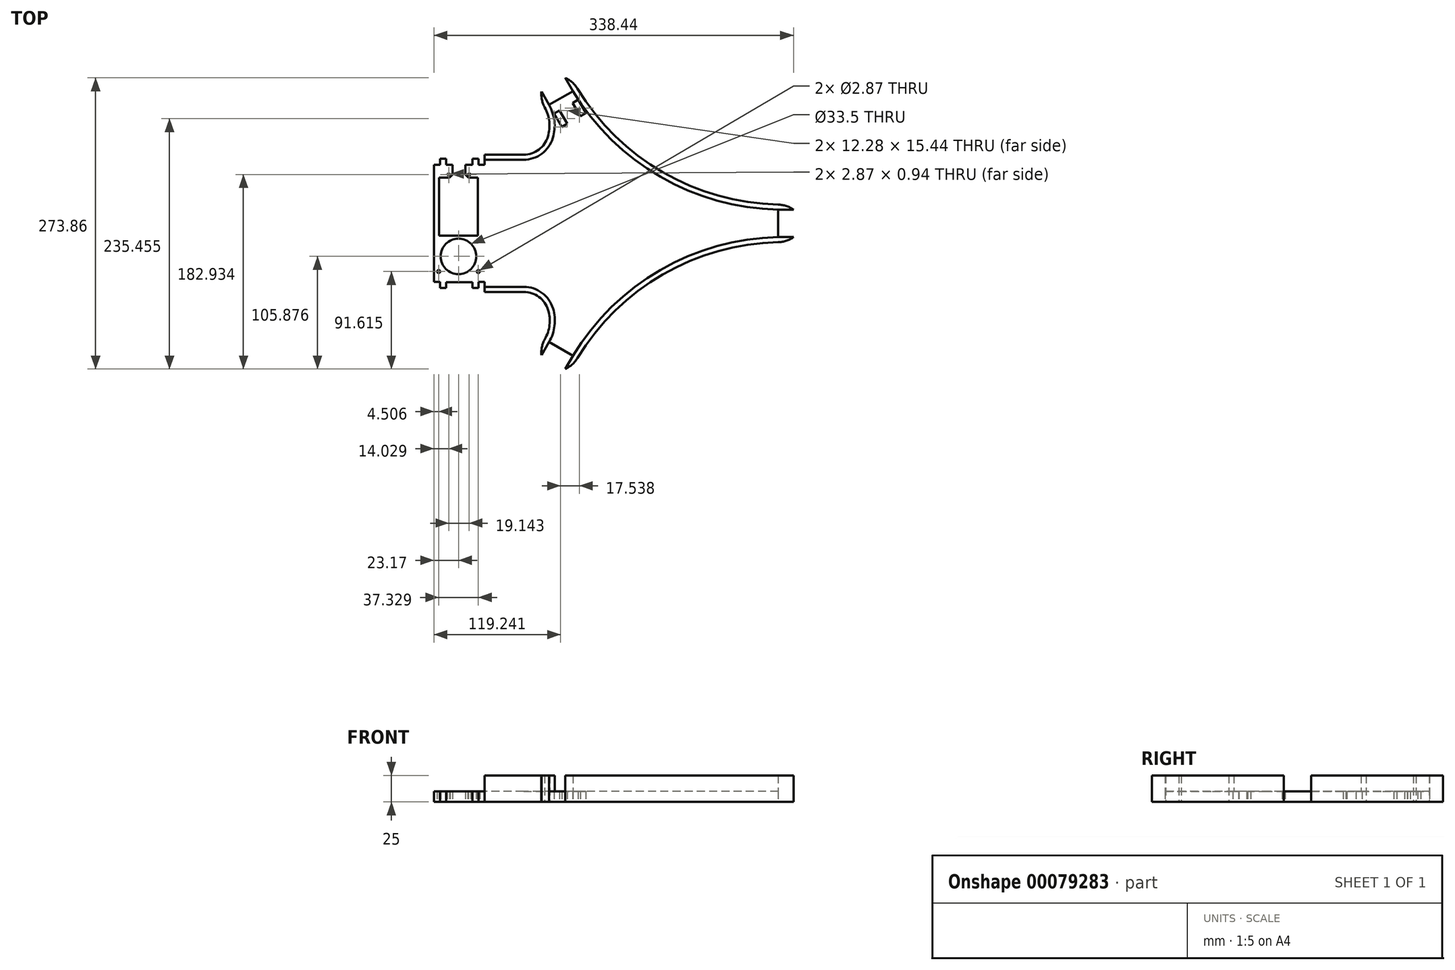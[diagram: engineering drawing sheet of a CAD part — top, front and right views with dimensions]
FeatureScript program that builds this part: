
annotation { "Feature Type Name" : "Feature", "Feature Type Description" : "" }
export const myFeature = defineFeature(function(context is Context, id is Id, definition is map)
    precondition{}
    {
        {
            var Q0;
            Q0=qCreatedBy(makeId("Top.planeOp"),FACE);
            var sketch = newSketch(context, id + "F0", { "sketchPlane" : qUnion([Q0])});
            skLineSegment(sketch, "E0", {"start": v(154.86, 12.92) * mm, "end": v(154.86, -12.92) * mm});
            skLineSegment(sketch, "E1", {"start": v(169.22, -12.92) * mm, "end": v(154.86, -12.92) * mm});
            skArc(sketch, "E2", {"start": v(154.86, -17.7) * mm, "mid": v(162.4, -16.4) * mm, "end": v(169.22, -12.92) * mm});
            skArc(sketch, "E3", {"start": v(154.86, -17.7) * mm, "mid": v(46.3, -48.05) * mm, "end": v(-34.25, -126.9) * mm});
            skArc(sketch, "E4", {"start": v(-45.57, -136.93) * mm, "mid": v(-39.15, -132.77) * mm, "end": v(-34.25, -126.9) * mm});
            skLineSegment(sketch, "E5", {"start": v(-45.57, -136.93) * mm, "end": v(-38.4, -124.5) * mm});
            skLineSegment(sketch, "E6", {"start": v(-38.4, -124.5) * mm, "end": v(-60.78, -111.58) * mm});
            skLineSegment(sketch, "E7", {"start": v(-67.95, -124.01) * mm, "end": v(-60.78, -111.58) * mm});
            skArc(sketch, "E8", {"start": v(-64.92, -109.18) * mm, "mid": v(-67.56, -116.37) * mm, "end": v(-67.95, -124.01) * mm});
            skArc(sketch, "E9", {"start": v(-64.92, -109.18) * mm, "mid": v(-60.4, -95.67) * mm, "end": v(-61.68, -81.48) * mm});
            skArc(sketch, "E10", {"start": v(-61.68, -81.48) * mm, "mid": v(-70.33, -69.23) * mm, "end": v(-84.57, -64.54) * mm});
            skLineSegment(sketch, "E11", {"start": v(-97.94, -64.54) * mm, "end": v(-84.57, -64.54) * mm});
            skLineSegment(sketch, "E12", {"start": v(-97.94, -64.54) * mm, "end": v(-121.43, -64.54) * mm});
            skLineSegment(sketch, "E13", {"start": v(-121.43, -55.04) * mm, "end": v(-121.43, -64.54) * mm});
            skLineSegment(sketch, "E14", {"start": v(-127.17, -55.04) * mm, "end": v(-121.43, -55.04) * mm});
            skLineSegment(sketch, "E15", {"start": v(-127.17, -60.78) * mm, "end": v(-127.17, -55.04) * mm});
            skLineSegment(sketch, "E16", {"start": v(-132.92, -60.78) * mm, "end": v(-127.17, -60.78) * mm});
            skLineSegment(sketch, "E17", {"start": v(-132.92, -55.45) * mm, "end": v(-132.92, -60.78) * mm});
            skLineSegment(sketch, "E18", {"start": v(-157.73, -55.45) * mm, "end": v(-132.92, -55.45) * mm});
            skLineSegment(sketch, "E19", {"start": v(-157.73, -55.45) * mm, "end": v(-157.73, -60.78) * mm});
            skLineSegment(sketch, "E20", {"start": v(-157.73, -60.78) * mm, "end": v(-163.48, -60.78) * mm});
            skLineSegment(sketch, "E21", {"start": v(-163.48, -60.78) * mm, "end": v(-163.48, -55.04) * mm});
            skLineSegment(sketch, "E22", {"start": v(-169.22, -55.04) * mm, "end": v(-163.48, -55.04) * mm});
            skLineSegment(sketch, "E23", {"start": v(-169.22, 55.04) * mm, "end": v(-169.22, -55.04) * mm});
            skLineSegment(sketch, "E24", {"start": v(-163.48, 55.04) * mm, "end": v(-169.22, 55.04) * mm});
            skLineSegment(sketch, "E25", {"start": v(-163.48, 60.78) * mm, "end": v(-163.48, 55.04) * mm});
            skLineSegment(sketch, "E26", {"start": v(-157.73, 60.78) * mm, "end": v(-163.48, 60.78) * mm});
            skLineSegment(sketch, "E27", {"start": v(-157.73, 55.04) * mm, "end": v(-157.73, 60.78) * mm});
            skLineSegment(sketch, "E28", {"start": v(-151.6, 55.04) * mm, "end": v(-157.73, 55.04) * mm});
            skLineSegment(sketch, "E29", {"start": v(-151.6, 50.17) * mm, "end": v(-151.6, 55.04) * mm});
            skLineSegment(sketch, "E30", {"start": v(-151.6, 50.17) * mm, "end": v(-151.6, 46) * mm});
            skArc(sketch, "E31", {"start": v(-154.47, 43.13) * mm, "mid": v(-152.44, 43.97) * mm, "end": v(-151.6, 46) * mm});
            skLineSegment(sketch, "E32", {"start": v(-164.24, 43.13) * mm, "end": v(-154.47, 43.13) * mm});
            skLineSegment(sketch, "E33", {"start": v(-164.24, -11.43) * mm, "end": v(-164.24, 43.13) * mm});
            skLineSegment(sketch, "E34", {"start": v(-127.86, -11.43) * mm, "end": v(-164.24, -11.43) * mm});
            skLineSegment(sketch, "E35", {"start": v(-127.86, 43.13) * mm, "end": v(-127.86, -11.43) * mm});
            skLineSegment(sketch, "E36", {"start": v(-136.77, 43.13) * mm, "end": v(-127.86, 43.13) * mm});
            skArc(sketch, "E37", {"start": v(-139.64, 46) * mm, "mid": v(-138.8, 43.97) * mm, "end": v(-136.77, 43.13) * mm});
            skLineSegment(sketch, "E38", {"start": v(-139.64, 46) * mm, "end": v(-139.64, 50.17) * mm});
            skLineSegment(sketch, "E39", {"start": v(-139.64, 50.17) * mm, "end": v(-139.64, 55.04) * mm});
            skLineSegment(sketch, "E40", {"start": v(-132.92, 55.04) * mm, "end": v(-139.64, 55.04) * mm});
            skLineSegment(sketch, "E41", {"start": v(-132.92, 55.04) * mm, "end": v(-132.92, 60.78) * mm});
            skLineSegment(sketch, "E42", {"start": v(-132.92, 60.78) * mm, "end": v(-127.17, 60.78) * mm});
            skLineSegment(sketch, "E43", {"start": v(-127.17, 60.78) * mm, "end": v(-127.17, 55.04) * mm});
            skLineSegment(sketch, "E44", {"start": v(-121.43, 55.04) * mm, "end": v(-127.17, 55.04) * mm});
            skLineSegment(sketch, "E45", {"start": v(-121.43, 64.68) * mm, "end": v(-121.43, 55.04) * mm});
            skLineSegment(sketch, "E46", {"start": v(-97.94, 64.68) * mm, "end": v(-121.43, 64.68) * mm});
            skLineSegment(sketch, "E47", {"start": v(-97.94, 64.68) * mm, "end": v(-84.8, 64.68) * mm});
            skArc(sketch, "E48", {"start": v(-84.8, 64.68) * mm, "mid": v(-70.5, 69.41) * mm, "end": v(-61.87, 81.74) * mm});
            skArc(sketch, "E49", {"start": v(-61.87, 81.74) * mm, "mid": v(-60.6, 95.77) * mm, "end": v(-64.92, 109.18) * mm});
            skArc(sketch, "E50", {"start": v(-67.95, 124.01) * mm, "mid": v(-67.56, 116.37) * mm, "end": v(-64.92, 109.18) * mm});
            skLineSegment(sketch, "E51", {"start": v(-67.95, 124.01) * mm, "end": v(-60.78, 111.58) * mm});
            skLineSegment(sketch, "E52", {"start": v(-60.78, 111.58) * mm, "end": v(-38.4, 124.5) * mm});
            skLineSegment(sketch, "E53", {"start": v(-45.57, 136.93) * mm, "end": v(-38.4, 124.5) * mm});
            skArc(sketch, "E54", {"start": v(-34.25, 126.9) * mm, "mid": v(-39.15, 132.77) * mm, "end": v(-45.57, 136.93) * mm});
            skArc(sketch, "E55", {"start": v(-34.25, 126.9) * mm, "mid": v(46.3, 48.05) * mm, "end": v(154.86, 17.7) * mm});
            skArc(sketch, "E56", {"start": v(169.22, 12.92) * mm, "mid": v(162.4, 16.4) * mm, "end": v(154.86, 17.7) * mm});
            skLineSegment(sketch, "E57", {"start": v(169.22, 12.92) * mm, "end": v(154.86, 12.92) * mm});
            skLineSegment(sketch, "E58", {"start": v(145.3, -13.02) * mm, "end": v(130.84, -13.02) * mm, "construction": true});
            skLineSegment(sketch, "E59", {"start": v(130.84, -13.02) * mm, "end": v(130.84, -7.18) * mm, "construction": true});
            skLineSegment(sketch, "E60", {"start": v(130.84, -7.18) * mm, "end": v(145.3, -7.18) * mm, "construction": true});
            skLineSegment(sketch, "E61", {"start": v(145.3, -7.18) * mm, "end": v(145.3, -13.02) * mm, "construction": true});
            skLineSegment(sketch, "E62", {"start": v(102.12, -13.02) * mm, "end": v(87.67, -13.02) * mm, "construction": true});
            skLineSegment(sketch, "E63", {"start": v(87.67, -13.02) * mm, "end": v(87.67, -7.18) * mm, "construction": true});
            skLineSegment(sketch, "E64", {"start": v(87.67, -7.18) * mm, "end": v(102.12, -7.18) * mm, "construction": true});
            skLineSegment(sketch, "E65", {"start": v(102.12, -7.18) * mm, "end": v(102.12, -13.02) * mm, "construction": true});
            skLineSegment(sketch, "E66", {"start": v(145.39, 13.02) * mm, "end": v(130.93, 13.02) * mm, "construction": true});
            skLineSegment(sketch, "E67", {"start": v(130.93, 13.02) * mm, "end": v(130.93, 7.18) * mm, "construction": true});
            skLineSegment(sketch, "E68", {"start": v(130.93, 7.18) * mm, "end": v(145.39, 7.18) * mm, "construction": true});
            skLineSegment(sketch, "E69", {"start": v(145.39, 7.18) * mm, "end": v(145.39, 13.02) * mm, "construction": true});
            skLineSegment(sketch, "E70", {"start": v(102.32, 13.02) * mm, "end": v(87.86, 13.02) * mm, "construction": true});
            skLineSegment(sketch, "E71", {"start": v(87.86, 13.02) * mm, "end": v(87.86, 7.18) * mm, "construction": true});
            skLineSegment(sketch, "E72", {"start": v(87.86, 7.18) * mm, "end": v(102.32, 7.18) * mm, "construction": true});
            skLineSegment(sketch, "E73", {"start": v(102.32, 7.18) * mm, "end": v(102.32, 13.02) * mm, "construction": true});
            skLineSegment(sketch, "E74", {"start": v(-76.97, 60.88) * mm, "end": v(-94.2, 60.88) * mm, "construction": true});
            skLineSegment(sketch, "E75", {"start": v(-94.2, 60.88) * mm, "end": v(-94.2, 55.04) * mm, "construction": true});
            skLineSegment(sketch, "E76", {"start": v(-94.2, 55.04) * mm, "end": v(-76.97, 55.04) * mm, "construction": true});
            skLineSegment(sketch, "E77", {"start": v(-76.97, 55.04) * mm, "end": v(-76.97, 60.88) * mm, "construction": true});
            skLineSegment(sketch, "E78", {"start": v(-76.97, -55.04) * mm, "end": v(-94.2, -55.04) * mm, "construction": true});
            skLineSegment(sketch, "E79", {"start": v(-94.2, -55.04) * mm, "end": v(-94.2, -60.88) * mm, "construction": true});
            skLineSegment(sketch, "E80", {"start": v(-94.2, -60.88) * mm, "end": v(-76.97, -60.88) * mm, "construction": true});
            skLineSegment(sketch, "E81", {"start": v(-76.97, -60.88) * mm, "end": v(-76.97, -55.04) * mm, "construction": true});
            skLineSegment(sketch, "E82", {"start": v(79.25, -1.44) * mm, "end": v(96.48, -1.44) * mm, "construction": true});
            skLineSegment(sketch, "E83", {"start": v(96.48, -1.44) * mm, "end": v(96.48, 1.44) * mm, "construction": true});
            skLineSegment(sketch, "E84", {"start": v(96.48, 1.44) * mm, "end": v(79.25, 1.44) * mm, "construction": true});
            skLineSegment(sketch, "E85", {"start": v(79.25, 1.44) * mm, "end": v(79.25, -1.44) * mm, "construction": true});
            skLineSegment(sketch, "E86", {"start": v(-137.48, 46.48) * mm, "end": v(-137.48, 45.53) * mm});
            skLineSegment(sketch, "E87", {"start": v(-137.48, 45.53) * mm, "end": v(-134.61, 45.53) * mm});
            skLineSegment(sketch, "E88", {"start": v(-134.61, 45.53) * mm, "end": v(-134.61, 46.48) * mm});
            skLineSegment(sketch, "E89", {"start": v(-134.61, 46.48) * mm, "end": v(-137.48, 46.48) * mm});
            skLineSegment(sketch, "E90", {"start": v(-156.63, 46.48) * mm, "end": v(-156.63, 45.53) * mm});
            skLineSegment(sketch, "E91", {"start": v(-156.63, 45.53) * mm, "end": v(-153.76, 45.53) * mm});
            skLineSegment(sketch, "E92", {"start": v(-153.76, 45.53) * mm, "end": v(-153.76, 46.48) * mm});
            skLineSegment(sketch, "E93", {"start": v(-153.76, 46.48) * mm, "end": v(-156.63, 46.48) * mm});
            skLineSegment(sketch, "E94", {"start": v(-34.48, 41.88) * mm, "end": v(-37.35, 44.75) * mm, "construction": true});
            skLineSegment(sketch, "E95", {"start": v(-37.35, 44.75) * mm, "end": v(-39.45, 44.75) * mm, "construction": true});
            skLineSegment(sketch, "E96", {"start": v(-39.45, 44.75) * mm, "end": v(-42.32, 47.62) * mm, "construction": true});
            skLineSegment(sketch, "E97", {"start": v(-42.32, 47.62) * mm, "end": v(-42.32, 49.63) * mm, "construction": true});
            skLineSegment(sketch, "E98", {"start": v(-42.32, 49.63) * mm, "end": v(-45.19, 52.5) * mm, "construction": true});
            skLineSegment(sketch, "E99", {"start": v(-45.19, 52.5) * mm, "end": v(-72.18, 52.5) * mm, "construction": true});
            skLineSegment(sketch, "E100", {"start": v(-72.18, 52.5) * mm, "end": v(-75.05, 49.63) * mm, "construction": true});
            skLineSegment(sketch, "E101", {"start": v(-75.05, 49.63) * mm, "end": v(-75.05, -49.63) * mm, "construction": true});
            skLineSegment(sketch, "E102", {"start": v(-75.05, -49.63) * mm, "end": v(-72.18, -52.5) * mm, "construction": true});
            skLineSegment(sketch, "E103", {"start": v(-72.18, -52.5) * mm, "end": v(-45.19, -52.5) * mm, "construction": true});
            skLineSegment(sketch, "E104", {"start": v(-45.19, -52.5) * mm, "end": v(-42.32, -49.63) * mm, "construction": true});
            skLineSegment(sketch, "E105", {"start": v(-42.32, -49.63) * mm, "end": v(-42.32, -47.62) * mm, "construction": true});
            skLineSegment(sketch, "E106", {"start": v(-42.32, -47.62) * mm, "end": v(-39.45, -44.75) * mm, "construction": true});
            skLineSegment(sketch, "E107", {"start": v(-39.45, -44.75) * mm, "end": v(-37.35, -44.75) * mm, "construction": true});
            skLineSegment(sketch, "E108", {"start": v(-37.35, -44.75) * mm, "end": v(-34.48, -41.88) * mm, "construction": true});
            skLineSegment(sketch, "E109", {"start": v(-34.48, -41.88) * mm, "end": v(-34.48, 41.88) * mm, "construction": true});
            skLineSegment(sketch, "E110", {"start": v(-103.77, 42.88) * mm, "end": v(-103.77, 49.63) * mm, "construction": true});
            skLineSegment(sketch, "E111", {"start": v(-103.77, 49.63) * mm, "end": v(-100.9, 52.5) * mm, "construction": true});
            skLineSegment(sketch, "E112", {"start": v(-100.9, 52.5) * mm, "end": v(-97.07, 52.5) * mm, "construction": true});
            skLineSegment(sketch, "E113", {"start": v(-97.07, 52.5) * mm, "end": v(-94.2, 49.63) * mm, "construction": true});
            skLineSegment(sketch, "E114", {"start": v(-94.2, 49.63) * mm, "end": v(-94.2, 42.88) * mm, "construction": true});
            skLineSegment(sketch, "E115", {"start": v(-94.2, 42.88) * mm, "end": v(-97.07, 40) * mm, "construction": true});
            skLineSegment(sketch, "E116", {"start": v(-97.07, 40) * mm, "end": v(-100.9, 40) * mm, "construction": true});
            skLineSegment(sketch, "E117", {"start": v(-100.9, 40) * mm, "end": v(-103.77, 42.88) * mm, "construction": true});
            skLineSegment(sketch, "E118", {"start": v(-103.77, 29.48) * mm, "end": v(-100.9, 32.35) * mm, "construction": true});
            skLineSegment(sketch, "E119", {"start": v(-100.9, 32.35) * mm, "end": v(-97.07, 32.35) * mm, "construction": true});
            skLineSegment(sketch, "E120", {"start": v(-97.07, 32.35) * mm, "end": v(-94.2, 29.48) * mm, "construction": true});
            skLineSegment(sketch, "E121", {"start": v(-94.2, 29.48) * mm, "end": v(-94.2, -41.88) * mm, "construction": true});
            skLineSegment(sketch, "E122", {"start": v(-94.2, -41.88) * mm, "end": v(-97.07, -44.75) * mm, "construction": true});
            skLineSegment(sketch, "E123", {"start": v(-97.07, -44.75) * mm, "end": v(-100.9, -44.75) * mm, "construction": true});
            skLineSegment(sketch, "E124", {"start": v(-100.9, -44.75) * mm, "end": v(-103.77, -41.88) * mm, "construction": true});
            skLineSegment(sketch, "E125", {"start": v(-103.77, -41.88) * mm, "end": v(-103.77, 29.48) * mm, "construction": true});
            skLineSegment(sketch, "E126", {"start": v(-42.43, -71.85) * mm, "end": v(-58.7, -71.85) * mm, "construction": true});
            skLineSegment(sketch, "E127", {"start": v(-58.7, -71.85) * mm, "end": v(-58.7, -68.98) * mm, "construction": true});
            skLineSegment(sketch, "E128", {"start": v(-58.7, -68.98) * mm, "end": v(-42.43, -68.98) * mm, "construction": true});
            skLineSegment(sketch, "E129", {"start": v(-42.43, -68.98) * mm, "end": v(-42.43, -71.85) * mm, "construction": true});
            skLineSegment(sketch, "E130", {"start": v(-9.77, 63.44) * mm, "end": v(-4.72, 66.36) * mm, "construction": true});
            skLineSegment(sketch, "E131", {"start": v(-4.72, 66.36) * mm, "end": v(-11.94, 78.87) * mm, "construction": true});
            skLineSegment(sketch, "E132", {"start": v(-11.94, 78.87) * mm, "end": v(-17, 75.95) * mm, "construction": true});
            skLineSegment(sketch, "E133", {"start": v(-17, 75.95) * mm, "end": v(-9.77, 63.44) * mm, "construction": true});
            skLineSegment(sketch, "E134", {"start": v(-21.64, 66.76) * mm, "end": v(-13.02, 51.84) * mm, "construction": true});
            skLineSegment(sketch, "E135", {"start": v(-13.02, 51.84) * mm, "end": v(-10.53, 53.27) * mm, "construction": true});
            skLineSegment(sketch, "E136", {"start": v(-10.53, 53.27) * mm, "end": v(-19.15, 68.2) * mm, "construction": true});
            skLineSegment(sketch, "E137", {"start": v(-19.15, 68.2) * mm, "end": v(-21.64, 66.76) * mm, "construction": true});
            skLineSegment(sketch, "E138", {"start": v(-34.58, 66.02) * mm, "end": v(-27.36, 53.5) * mm, "construction": true});
            skLineSegment(sketch, "E139", {"start": v(-27.36, 53.5) * mm, "end": v(-22.3, 56.42) * mm, "construction": true});
            skLineSegment(sketch, "E140", {"start": v(-22.3, 56.42) * mm, "end": v(-29.53, 68.94) * mm, "construction": true});
            skLineSegment(sketch, "E141", {"start": v(-29.53, 68.94) * mm, "end": v(-34.58, 66.02) * mm, "construction": true});
            skLineSegment(sketch, "E142", {"start": v(-26.3, 103.74) * mm, "end": v(-33.53, 116.26) * mm});
            skLineSegment(sketch, "E143", {"start": v(-33.53, 116.26) * mm, "end": v(-38.58, 113.34) * mm});
            skLineSegment(sketch, "E144", {"start": v(-38.58, 113.34) * mm, "end": v(-31.36, 100.82) * mm});
            skLineSegment(sketch, "E145", {"start": v(-31.36, 100.82) * mm, "end": v(-26.3, 103.74) * mm});
            skLineSegment(sketch, "E146", {"start": v(-43.84, 93.73) * mm, "end": v(-48.9, 90.8) * mm});
            skLineSegment(sketch, "E147", {"start": v(-48.9, 90.8) * mm, "end": v(-56.12, 103.32) * mm});
            skLineSegment(sketch, "E148", {"start": v(-56.12, 103.32) * mm, "end": v(-51.06, 106.24) * mm});
            skLineSegment(sketch, "E149", {"start": v(-51.06, 106.24) * mm, "end": v(-43.84, 93.73) * mm});
            skLineSegment(sketch, "E150", {"start": v(-17.1, -76.12) * mm, "end": v(-9.87, -63.6) * mm, "construction": true});
            skLineSegment(sketch, "E151", {"start": v(-9.87, -63.6) * mm, "end": v(-4.81, -66.52) * mm, "construction": true});
            skLineSegment(sketch, "E152", {"start": v(-4.81, -66.52) * mm, "end": v(-12.04, -79.04) * mm, "construction": true});
            skLineSegment(sketch, "E153", {"start": v(-12.04, -79.04) * mm, "end": v(-17.1, -76.12) * mm, "construction": true});
            skLineSegment(sketch, "E154", {"start": v(-51.02, -106.16) * mm, "end": v(-43.79, -93.64) * mm, "construction": true});
            skLineSegment(sketch, "E155", {"start": v(-43.79, -93.64) * mm, "end": v(-48.85, -90.72) * mm, "construction": true});
            skLineSegment(sketch, "E156", {"start": v(-48.85, -90.72) * mm, "end": v(-56.07, -103.24) * mm, "construction": true});
            skLineSegment(sketch, "E157", {"start": v(-56.07, -103.24) * mm, "end": v(-51.02, -106.16) * mm, "construction": true});
            skLineSegment(sketch, "E158", {"start": v(-34.49, -65.86) * mm, "end": v(-27.26, -53.34) * mm, "construction": true});
            skLineSegment(sketch, "E159", {"start": v(-27.26, -53.34) * mm, "end": v(-22.2, -56.26) * mm, "construction": true});
            skLineSegment(sketch, "E160", {"start": v(-22.2, -56.26) * mm, "end": v(-29.43, -68.78) * mm, "construction": true});
            skLineSegment(sketch, "E161", {"start": v(-29.43, -68.78) * mm, "end": v(-34.49, -65.86) * mm, "construction": true});
            skLineSegment(sketch, "E162", {"start": v(-19.15, -68.2) * mm, "end": v(-10.53, -53.27) * mm, "construction": true});
            skLineSegment(sketch, "E163", {"start": v(-10.53, -53.27) * mm, "end": v(-13.02, -51.84) * mm, "construction": true});
            skLineSegment(sketch, "E164", {"start": v(-13.02, -51.84) * mm, "end": v(-21.64, -66.76) * mm, "construction": true});
            skLineSegment(sketch, "E165", {"start": v(-21.64, -66.76) * mm, "end": v(-19.15, -68.2) * mm, "construction": true});
            skLineSegment(sketch, "E166", {"start": v(-31.4, -100.9) * mm, "end": v(-26.35, -103.82) * mm, "construction": true});
            skLineSegment(sketch, "E167", {"start": v(-26.35, -103.82) * mm, "end": v(-33.57, -116.34) * mm, "construction": true});
            skLineSegment(sketch, "E168", {"start": v(-33.57, -116.34) * mm, "end": v(-38.63, -113.42) * mm, "construction": true});
            skLineSegment(sketch, "E169", {"start": v(-38.63, -113.42) * mm, "end": v(-31.4, -100.9) * mm, "construction": true});
            skLineSegment(sketch, "E170", {"start": v(-163.48, -55.04) * mm, "end": v(-163.48, -60.78) * mm});
            skLineSegment(sketch, "E171", {"start": v(-163.48, -60.78) * mm, "end": v(-157.73, -60.78) * mm});
            skLineSegment(sketch, "E172", {"start": v(-157.73, -60.78) * mm, "end": v(-157.73, -55.45) * mm});
            skLineSegment(sketch, "E173", {"start": v(-121.43, -64.54) * mm, "end": v(-97.94, -64.54) * mm});
            skLineSegment(sketch, "E174", {"start": v(-84.57, -64.54) * mm, "end": v(-61.68, -81.48) * mm});
            skLineSegment(sketch, "E175", {"start": v(-61.68, -81.48) * mm, "end": v(-64.92, -109.18) * mm});
            skLineSegment(sketch, "E176", {"start": v(-64.92, -109.18) * mm, "end": v(-67.95, -124.01) * mm});
            skLineSegment(sketch, "E177", {"start": v(-60.78, -111.58) * mm, "end": v(-38.4, -124.5) * mm});
            skLineSegment(sketch, "E178", {"start": v(-38.4, -124.5) * mm, "end": v(-45.57, -136.93) * mm});
            skLineSegment(sketch, "E179", {"start": v(-45.57, -136.93) * mm, "end": v(-34.25, -126.9) * mm});
            skLineSegment(sketch, "E180", {"start": v(-34.25, -126.9) * mm, "end": v(154.86, -17.7) * mm});
            skLineSegment(sketch, "E181", {"start": v(154.86, -17.7) * mm, "end": v(169.22, -12.92) * mm});
            skLineSegment(sketch, "E182", {"start": v(154.86, -12.92) * mm, "end": v(154.86, 12.92) * mm});
            skLineSegment(sketch, "E183", {"start": v(154.86, 12.92) * mm, "end": v(169.22, 12.92) * mm});
            skLineSegment(sketch, "E184", {"start": v(169.22, 12.92) * mm, "end": v(154.86, 17.7) * mm});
            skLineSegment(sketch, "E185", {"start": v(154.86, 17.7) * mm, "end": v(-34.25, 126.9) * mm});
            skLineSegment(sketch, "E186", {"start": v(-34.25, 126.9) * mm, "end": v(-45.57, 136.93) * mm});
            skLineSegment(sketch, "E187", {"start": v(-38.4, 124.5) * mm, "end": v(-60.78, 111.58) * mm});
            skLineSegment(sketch, "E188", {"start": v(-60.78, 111.58) * mm, "end": v(-67.95, 124.01) * mm});
            skLineSegment(sketch, "E189", {"start": v(-67.95, 124.01) * mm, "end": v(-64.92, 109.18) * mm});
            skLineSegment(sketch, "E190", {"start": v(-64.92, 109.18) * mm, "end": v(-61.87, 81.74) * mm});
            skLineSegment(sketch, "E191", {"start": v(-61.87, 81.74) * mm, "end": v(-84.8, 64.68) * mm});
            skLineSegment(sketch, "E192", {"start": v(-84.8, 64.68) * mm, "end": v(-97.94, 64.68) * mm});
            skLineSegment(sketch, "E193", {"start": v(-127.17, 55.04) * mm, "end": v(-127.17, 60.78) * mm});
            skLineSegment(sketch, "E194", {"start": v(-127.17, 60.78) * mm, "end": v(-132.92, 60.78) * mm});
            skLineSegment(sketch, "E195", {"start": v(-132.92, 60.78) * mm, "end": v(-132.92, 55.04) * mm});
            skLineSegment(sketch, "E196", {"start": v(-139.64, 55.04) * mm, "end": v(-139.64, 50.17) * mm});
            skLineSegment(sketch, "E197", {"start": v(-99.85, 48.62) * mm, "end": v(-38.4, 48.62) * mm, "construction": true});
            skLineSegment(sketch, "E198", {"start": v(-38.4, 48.62) * mm, "end": v(-38.4, -48.62) * mm, "construction": true});
            skLineSegment(sketch, "E199", {"start": v(-38.4, -48.62) * mm, "end": v(-99.85, -48.62) * mm, "construction": true});
            skLineSegment(sketch, "E200", {"start": v(-139.64, 50.17) * mm, "end": v(-139.64, 46) * mm});
            skLineSegment(sketch, "E201", {"start": v(-139.64, 46) * mm, "end": v(-136.77, 43.13) * mm});
            skLineSegment(sketch, "E202", {"start": v(-154.47, 43.13) * mm, "end": v(-151.6, 46) * mm});
            skLineSegment(sketch, "E203", {"start": v(-151.6, 46) * mm, "end": v(-151.6, 50.17) * mm});
            skLineSegment(sketch, "E204", {"start": v(-151.6, 50.17) * mm, "end": v(-156.63, 50.17) * mm});
            skLineSegment(sketch, "E205", {"start": v(-156.63, 50.17) * mm, "end": v(-158.25, 47.84) * mm});
            skLineSegment(sketch, "E206", {"start": v(-158.25, 47.84) * mm, "end": v(-167.44, 47.84) * mm});
            skLineSegment(sketch, "E207", {"start": v(-167.44, 47.84) * mm, "end": v(-167.44, -47.87) * mm});
            skLineSegment(sketch, "E208", {"start": v(-167.44, -47.87) * mm, "end": v(-158.3, -47.87) * mm});
            skLineSegment(sketch, "E209", {"start": v(-132.29, -47.95) * mm, "end": v(-134.61, -50.27) * mm});
            skLineSegment(sketch, "E210", {"start": v(-134.61, -50.27) * mm, "end": v(-156.63, -50.27) * mm});
            skLineSegment(sketch, "E211", {"start": v(-156.63, -50.27) * mm, "end": v(-158.25, -47.95) * mm});
            skLineSegment(sketch, "E212", {"start": v(-132.21, -47.87) * mm, "end": v(-123.8, -47.87) * mm});
            skLineSegment(sketch, "E213", {"start": v(-123.8, -47.87) * mm, "end": v(-123.8, 47.84) * mm});
            skLineSegment(sketch, "E214", {"start": v(-123.8, 47.84) * mm, "end": v(-132.29, 47.84) * mm});
            skLineSegment(sketch, "E215", {"start": v(-132.29, 47.84) * mm, "end": v(-134.61, 50.17) * mm});
            skCircle(sketch, "E216", {"center": v(18.56, 0) * mm, "radius": 1.44 * mm, "construction": true});
            skLineSegment(sketch, "E217", {"start": v(22.08, -23.58) * mm, "end": v(-18.45, -34.44) * mm, "construction": true});
            skCircle(sketch, "E218", {"center": v(-18.45, -34.44) * mm, "radius": 1.44 * mm, "construction": true});
            skLineSegment(sketch, "E219", {"start": v(7.24, -49.28) * mm, "end": v(-3.62, -8.75) * mm, "construction": true});
            skCircle(sketch, "E220", {"center": v(1.81, -29.01) * mm, "radius": 14.36 * mm, "construction": true});
            skCircle(sketch, "E221", {"center": v(7.24, -49.28) * mm, "radius": 1.44 * mm, "construction": true});
            skLineSegment(sketch, "E222", {"start": v(29.47, -21.6) * mm, "end": v(9.22, -56.67) * mm, "construction": true});
            skLineSegment(sketch, "E223", {"start": v(29.47, -21.6) * mm, "end": v(-25.84, -36.42) * mm, "construction": true});
            skLineSegment(sketch, "E224", {"start": v(9.22, -56.67) * mm, "end": v(-5.6, -1.36) * mm, "construction": true});
            skLineSegment(sketch, "E225", {"start": v(9.22, -56.67) * mm, "end": v(-25.84, -36.42) * mm, "construction": true});
            skLineSegment(sketch, "E226", {"start": v(-5.6, -1.36) * mm, "end": v(29.47, -21.6) * mm, "construction": true});
            skCircle(sketch, "E227", {"center": v(-29.76, -52.12) * mm, "radius": 1.44 * mm, "construction": true});
            skLineSegment(sketch, "E228", {"start": v(-25.84, -36.42) * mm, "end": v(-5.6, -1.36) * mm, "construction": true});
            skCircle(sketch, "E229", {"center": v(-2.4, -67.91) * mm, "radius": 1.44 * mm, "construction": true});
            skCircle(sketch, "E230", {"center": v(22.08, -23.58) * mm, "radius": 1.44 * mm, "construction": true});
            skCircle(sketch, "E231", {"center": v(-3.62, -8.75) * mm, "radius": 1.44 * mm, "construction": true});
            skLineSegment(sketch, "E232", {"start": v(-35.26, 48.94) * mm, "end": v(2.62, 70.82) * mm, "construction": true});
            skCircle(sketch, "E233", {"center": v(-29.76, 52.12) * mm, "radius": 1.44 * mm, "construction": true});
            skLineSegment(sketch, "E234", {"start": v(29.47, 21.6) * mm, "end": v(-5.6, 1.36) * mm, "construction": true});
            skCircle(sketch, "E235", {"center": v(-3.62, 8.75) * mm, "radius": 1.44 * mm, "construction": true});
            skCircle(sketch, "E236", {"center": v(22.08, 23.58) * mm, "radius": 1.44 * mm, "construction": true});
            skLineSegment(sketch, "E237", {"start": v(-25.84, 36.42) * mm, "end": v(9.22, 56.67) * mm, "construction": true});
            skLineSegment(sketch, "E238", {"start": v(-25.84, 36.42) * mm, "end": v(29.47, 21.6) * mm, "construction": true});
            skLineSegment(sketch, "E239", {"start": v(-5.6, 1.36) * mm, "end": v(9.22, 56.67) * mm, "construction": true});
            skLineSegment(sketch, "E240", {"start": v(-5.6, 1.36) * mm, "end": v(-25.84, 36.42) * mm, "construction": true});
            skCircle(sketch, "E241", {"center": v(-18.45, 34.44) * mm, "radius": 1.44 * mm, "construction": true});
            skLineSegment(sketch, "E242", {"start": v(-18.45, 34.44) * mm, "end": v(22.08, 23.58) * mm, "construction": true});
            skLineSegment(sketch, "E243", {"start": v(-3.62, 8.75) * mm, "end": v(7.24, 49.28) * mm, "construction": true});
            skCircle(sketch, "E244", {"center": v(1.81, 29.01) * mm, "radius": 14.36 * mm, "construction": true});
            skCircle(sketch, "E245", {"center": v(7.24, 49.28) * mm, "radius": 1.44 * mm, "construction": true});
            skLineSegment(sketch, "E246", {"start": v(9.22, 56.67) * mm, "end": v(29.47, 21.6) * mm, "construction": true});
            skCircle(sketch, "E247", {"center": v(-2.4, 67.91) * mm, "radius": 1.44 * mm, "construction": true});
            skLineSegment(sketch, "E248", {"start": v(-99.85, -48.62) * mm, "end": v(-38.4, 48.62) * mm, "construction": true});
            skLineSegment(sketch, "E249", {"start": v(-38.4, -48.62) * mm, "end": v(-69.12, 0) * mm, "construction": true});
            skLineSegment(sketch, "E250", {"start": v(-103.77, -44.75) * mm, "end": v(-95.93, -52.5) * mm, "construction": true});
            skLineSegment(sketch, "E251", {"start": v(-95.93, -44.75) * mm, "end": v(-103.77, -52.5) * mm, "construction": true});
            skLineSegment(sketch, "E252", {"start": v(-34.48, -44.75) * mm, "end": v(-42.32, -52.5) * mm, "construction": true});
            skLineSegment(sketch, "E253", {"start": v(-42.32, -44.75) * mm, "end": v(-34.48, -52.5) * mm, "construction": true});
            skCircle(sketch, "E254", {"center": v(-38.4, -48.62) * mm, "radius": 1.44 * mm, "construction": true});
            skCircle(sketch, "E255", {"center": v(-99.85, -48.62) * mm, "radius": 1.44 * mm, "construction": true});
            skLineSegment(sketch, "E256", {"start": v(-34.48, 44.75) * mm, "end": v(-42.32, 52.5) * mm, "construction": true});
            skLineSegment(sketch, "E257", {"start": v(-42.32, 44.75) * mm, "end": v(-34.48, 52.5) * mm, "construction": true});
            skLineSegment(sketch, "E258", {"start": v(-103.77, 40) * mm, "end": v(-95.92, 32.35) * mm, "construction": true});
            skLineSegment(sketch, "E259", {"start": v(-95.92, 40) * mm, "end": v(-103.77, 32.35) * mm, "construction": true});
            skLineSegment(sketch, "E260", {"start": v(-99.85, -49.58) * mm, "end": v(-99.85, -45.75) * mm, "construction": true});
            skLineSegment(sketch, "E261", {"start": v(-38.4, -49.58) * mm, "end": v(-38.4, -45.75) * mm, "construction": true});
            skLineSegment(sketch, "E262", {"start": v(-155.2, 46.48) * mm, "end": v(-155.2, 45.53) * mm});
            skLineSegment(sketch, "E263", {"start": v(-136.05, 46.48) * mm, "end": v(-136.05, 45.53) * mm});
            skCircle(sketch, "E264", {"center": v(87.86, -15.8) * mm, "radius": 1.44 * mm, "construction": true});
            skCircle(sketch, "E265", {"center": v(87.86, 15.8) * mm, "radius": 1.44 * mm, "construction": true});
            skLineSegment(sketch, "E266", {"start": v(87.86, 22.15) * mm, "end": v(87.86, -21.6) * mm, "construction": true});
            skCircle(sketch, "E267", {"center": v(-21.09, -9.57) * mm, "radius": 1.44 * mm, "construction": true});
            skCircle(sketch, "E268", {"center": v(-21.09, 9.57) * mm, "radius": 1.44 * mm, "construction": true});
            skLineSegment(sketch, "E269", {"start": v(-106.3, 64.68) * mm, "end": v(-106.3, 33.5) * mm, "construction": true});
            skLineSegment(sketch, "E270", {"start": v(-106.3, 31.73) * mm, "end": v(-106.3, 1.1) * mm, "construction": true});
            skLineSegment(sketch, "E271", {"start": v(-106.3, -0.67) * mm, "end": v(-106.3, -31.3) * mm, "construction": true});
            skLineSegment(sketch, "E272", {"start": v(-106.3, -33.07) * mm, "end": v(-106.3, -64.13) * mm, "construction": true});
            skLineSegment(sketch, "E273", {"start": v(-107.82, 48.81) * mm, "end": v(-107.82, 18.19) * mm, "construction": true});
            skLineSegment(sketch, "E274", {"start": v(-107.82, 16.42) * mm, "end": v(-107.82, -14.21) * mm, "construction": true});
            skLineSegment(sketch, "E275", {"start": v(-107.82, -15.98) * mm, "end": v(-107.82, -46.61) * mm, "construction": true});
            skLineSegment(sketch, "E276", {"start": v(-109.33, 64.68) * mm, "end": v(-109.33, 33.5) * mm, "construction": true});
            skLineSegment(sketch, "E277", {"start": v(-109.33, 31.73) * mm, "end": v(-109.33, 1.1) * mm, "construction": true});
            skLineSegment(sketch, "E278", {"start": v(-109.33, -0.67) * mm, "end": v(-109.33, -31.3) * mm, "construction": true});
            skLineSegment(sketch, "E279", {"start": v(-109.33, -33.07) * mm, "end": v(-109.33, -64.13) * mm, "construction": true});
            skLineSegment(sketch, "E280", {"start": v(-110.84, 48.81) * mm, "end": v(-110.84, 18.19) * mm, "construction": true});
            skLineSegment(sketch, "E281", {"start": v(-110.84, 16.42) * mm, "end": v(-110.84, -14.21) * mm, "construction": true});
            skLineSegment(sketch, "E282", {"start": v(-110.84, -15.98) * mm, "end": v(-110.84, -46.61) * mm, "construction": true});
            skLineSegment(sketch, "E283", {"start": v(-112.36, 64.68) * mm, "end": v(-112.36, 33.5) * mm, "construction": true});
            skLineSegment(sketch, "E284", {"start": v(-112.36, 31.73) * mm, "end": v(-112.36, 1.1) * mm, "construction": true});
            skLineSegment(sketch, "E285", {"start": v(-112.36, -0.67) * mm, "end": v(-112.36, -31.3) * mm, "construction": true});
            skLineSegment(sketch, "E286", {"start": v(-112.36, -33.07) * mm, "end": v(-112.36, -64.54) * mm, "construction": true});
            skLineSegment(sketch, "E287", {"start": v(-113.87, 48.81) * mm, "end": v(-113.87, 18.19) * mm, "construction": true});
            skLineSegment(sketch, "E288", {"start": v(-113.87, 16.42) * mm, "end": v(-113.87, -14.21) * mm, "construction": true});
            skLineSegment(sketch, "E289", {"start": v(-113.87, -15.98) * mm, "end": v(-113.87, -46.61) * mm, "construction": true});
            skLineSegment(sketch, "E290", {"start": v(-115.38, 64.68) * mm, "end": v(-115.38, 33.5) * mm, "construction": true});
            skLineSegment(sketch, "E291", {"start": v(-115.38, 31.73) * mm, "end": v(-115.38, 1.1) * mm, "construction": true});
            skLineSegment(sketch, "E292", {"start": v(-115.38, -0.67) * mm, "end": v(-115.38, -31.3) * mm, "construction": true});
            skLineSegment(sketch, "E293", {"start": v(-115.38, -33.07) * mm, "end": v(-115.38, -64.54) * mm, "construction": true});
            skLineSegment(sketch, "E294", {"start": v(-116.9, 48.81) * mm, "end": v(-116.9, 18.19) * mm, "construction": true});
            skLineSegment(sketch, "E295", {"start": v(-116.9, 16.42) * mm, "end": v(-116.9, -14.21) * mm, "construction": true});
            skLineSegment(sketch, "E296", {"start": v(-116.9, -15.98) * mm, "end": v(-116.9, -46.61) * mm, "construction": true});
            skLineSegment(sketch, "E297", {"start": v(-118.4, 64.68) * mm, "end": v(-118.4, 33.5) * mm, "construction": true});
            skLineSegment(sketch, "E298", {"start": v(-118.4, 31.73) * mm, "end": v(-118.4, 1.1) * mm, "construction": true});
            skLineSegment(sketch, "E299", {"start": v(-118.4, -0.67) * mm, "end": v(-118.4, -31.3) * mm, "construction": true});
            skLineSegment(sketch, "E300", {"start": v(-118.4, -33.07) * mm, "end": v(-118.4, -64.54) * mm, "construction": true});
            skLineSegment(sketch, "E301", {"start": v(-119.92, 48.81) * mm, "end": v(-119.92, 18.19) * mm, "construction": true});
            skLineSegment(sketch, "E302", {"start": v(-119.92, 16.42) * mm, "end": v(-119.92, -14.21) * mm, "construction": true});
            skLineSegment(sketch, "E303", {"start": v(-119.92, -15.98) * mm, "end": v(-119.92, -46.61) * mm, "construction": true});
            skLineSegment(sketch, "E304", {"start": v(-121.43, -1.08) * mm, "end": v(-121.43, -31.7) * mm, "construction": true});
            skLineSegment(sketch, "E305", {"start": v(-121.43, 31.73) * mm, "end": v(-121.43, 1.1) * mm, "construction": true});
            skLineSegment(sketch, "E306", {"start": v(-134.61, 50.17) * mm, "end": v(-139.64, 50.17) * mm});
            skLineSegment(sketch, "E307", {"start": v(-134.61, 50.17) * mm, "end": v(-131.33, 50.17) * mm});
            skCircle(sketch, "E308", {"center": v(-164.71, -45.32) * mm, "radius": 1.44 * mm});
            skCircle(sketch, "E309", {"center": v(-127.39, -45.32) * mm, "radius": 1.44 * mm});
            skCircle(sketch, "E310", {"center": v(-146.05, -31.05) * mm, "radius": 16.75 * mm});
            skLineSegment(sketch, "E311", {"start": v(72.3, 20.24) * mm, "end": v(31.82, -20.24) * mm, "construction": true});
            skLineSegment(sketch, "E312", {"start": v(31.82, 20.24) * mm, "end": v(72.3, -20.24) * mm, "construction": true});
            skLineSegment(sketch, "E313", {"start": v(31.82, -20.24) * mm, "end": v(31.82, 20.24) * mm, "construction": true});
            skLineSegment(sketch, "E314", {"start": v(72.3, -20.24) * mm, "end": v(31.82, -20.24) * mm, "construction": true});
            skLineSegment(sketch, "E315", {"start": v(72.3, 20.24) * mm, "end": v(72.3, -20.24) * mm, "construction": true});
            skLineSegment(sketch, "E316", {"start": v(31.82, 20.24) * mm, "end": v(72.3, 20.24) * mm, "construction": true});
            skCircle(sketch, "E317", {"center": v(-99.85, 36.18) * mm, "radius": 1.44 * mm, "construction": true});
            skCircle(sketch, "E318", {"center": v(-38.4, 48.62) * mm, "radius": 1.44 * mm, "construction": true});
            skLineSegment(sketch, "E319", {"start": v(-99.85, -48.62) * mm, "end": v(-99.85, 48.62) * mm, "construction": true});
            skCircle(sketch, "E320", {"center": v(42.95, 42.24) * mm, "radius": 1.91 * mm, "construction": true});
            skCircle(sketch, "E321", {"center": v(44.7, 35.7) * mm, "radius": 1.91 * mm, "construction": true});
            skCircle(sketch, "E322", {"center": v(36.41, 40.49) * mm, "radius": 1.91 * mm, "construction": true});
            skCircle(sketch, "E323", {"center": v(38.16, 33.95) * mm, "radius": 1.91 * mm, "construction": true});
            skCircle(sketch, "E324", {"center": v(42.95, -42.24) * mm, "radius": 1.91 * mm, "construction": true});
            skCircle(sketch, "E325", {"center": v(36.41, -40.49) * mm, "radius": 1.91 * mm, "construction": true});
            skCircle(sketch, "E326", {"center": v(44.7, -35.7) * mm, "radius": 1.91 * mm, "construction": true});
            skCircle(sketch, "E327", {"center": v(38.16, -33.95) * mm, "radius": 1.91 * mm, "construction": true});
            skCircle(sketch, "E328", {"center": v(37.23, -14.84) * mm, "radius": 1.44 * mm, "construction": true});
            skCircle(sketch, "E329", {"center": v(37.23, 14.84) * mm, "radius": 1.44 * mm, "construction": true});
            skCircle(sketch, "E330", {"center": v(66.9, 14.84) * mm, "radius": 1.44 * mm, "construction": true});
            skCircle(sketch, "E331", {"center": v(66.9, -14.84) * mm, "radius": 1.44 * mm, "construction": true});
            skLineSegment(sketch, "E332", {"start": v(66.9, 14.84) * mm, "end": v(37.23, -14.84) * mm, "construction": true});
            skLineSegment(sketch, "E333", {"start": v(37.23, 14.84) * mm, "end": v(66.9, -14.84) * mm, "construction": true});
            skCircle(sketch, "E334", {"center": v(52.06, 0) * mm, "radius": 14.36 * mm, "construction": true});
            skArc(sketch, "E335", {"start": v(-38.4, 124.5) * mm, "mid": v(43.91, 43.9) * mm, "end": v(154.86, 12.92) * mm});
            skArc(sketch, "E336", {"start": v(154.86, -12.92) * mm, "mid": v(43.91, -43.9) * mm, "end": v(-38.4, -124.5) * mm});
            skLineSegment(sketch, "E337.0", {"start": v(-97.94, -59.75) * mm, "end": v(-121.43, -59.75) * mm});
            skLineSegment(sketch, "E337.1", {"start": v(-97.94, -59.75) * mm, "end": v(-84.57, -59.75) * mm});
            skArc(sketch, "E337.2", {"start": v(-57.1, -80.08) * mm, "mid": v(-67.48, -65.39) * mm, "end": v(-84.57, -59.75) * mm});
            skArc(sketch, "E337.3", {"start": v(-60.79, -111.6) * mm, "mid": v(-55.65, -96.23) * mm, "end": v(-57.1, -80.08) * mm});
            skArc(sketch, "E338.0", {"start": v(-57.29, 80.37) * mm, "mid": v(-55.85, 96.33) * mm, "end": v(-60.78, 111.58) * mm});
            skArc(sketch, "E338.1", {"start": v(-84.8, 59.9) * mm, "mid": v(-67.65, 65.57) * mm, "end": v(-57.29, 80.37) * mm});
            skLineSegment(sketch, "E338.2", {"start": v(-84.8, 59.9) * mm, "end": v(-97.94, 59.9) * mm});
            skLineSegment(sketch, "E338.3", {"start": v(-97.94, 59.9) * mm, "end": v(-121.43, 59.9) * mm});
            skSolve(sketch);
        }
        {
            var Q0;
            {var subQ17=sQuery(id+"F0.wireOp",EDGE,"E86");Q0=makeQuery(id+"F0.imprint","IMPRINT",FACE,{"disambiguationData":[TD([[makeQuery(id+"F0.imprint","IMPRINT",EDGE,{"derivedFrom":subQ17}),-1.0]])]});}
            extrude(context, id + "F1", {"entities" : qUnion([Q0]), "depth" : 10 * mm});
        }
        {
            var Q0;
            Q0=makeQuery(id+"F0.imprint","IMPRINT",FACE,{"disambiguationData":[TD([[makeQuery(id+"F0.imprint","IMPRINT",EDGE,{"derivedFrom":sQuery(id+"F0.wireOp",EDGE,"E9")}),-1.0]])]});
            var Q1;
            Q1=makeQuery(id+"F0.imprint","IMPRINT",FACE,{"disambiguationData":[TD([[makeQuery(id+"F0.imprint","IMPRINT",EDGE,{"derivedFrom":sQuery(id+"F0.wireOp",EDGE,"E8")}),1.0]])]});
            var Q2;
            Q2=makeQuery(id+"F0.imprint","IMPRINT",FACE,{"disambiguationData":[TD([[makeQuery(id+"F0.imprint","IMPRINT",EDGE,{"derivedFrom":sQuery(id+"F0.wireOp",EDGE,"E4")}),1.0]])]});
            var Q3;
            Q3=makeQuery(id+"F0.imprint","IMPRINT",FACE,{"disambiguationData":[TD([[makeQuery(id+"F0.imprint","IMPRINT",EDGE,{"derivedFrom":sQuery(id+"F0.wireOp",EDGE,"E3")}),-1.0]])]});
            var Q4;
            Q4=makeQuery(id+"F0.imprint","IMPRINT",FACE,{"disambiguationData":[TD([[makeQuery(id+"F0.imprint","IMPRINT",EDGE,{"derivedFrom":sQuery(id+"F0.wireOp",EDGE,"E2")}),1.0]])]});
            var Q5;
            Q5=makeQuery(id+"F0.imprint","IMPRINT",FACE,{"disambiguationData":[TD([[makeQuery(id+"F0.imprint","IMPRINT",EDGE,{"derivedFrom":sQuery(id+"F0.wireOp",EDGE,"E56")}),1.0]])]});
            var Q6;
            Q6=makeQuery(id+"F0.imprint","IMPRINT",FACE,{"disambiguationData":[TD([[makeQuery(id+"F0.imprint","IMPRINT",EDGE,{"derivedFrom":sQuery(id+"F0.wireOp",EDGE,"E55")}),-1.0]])]});
            var Q7;
            Q7=makeQuery(id+"F0.imprint","IMPRINT",FACE,{"disambiguationData":[TD([[makeQuery(id+"F0.imprint","IMPRINT",EDGE,{"derivedFrom":sQuery(id+"F0.wireOp",EDGE,"E54")}),1.0]])]});
            var Q8;
            Q8=makeQuery(id+"F0.imprint","IMPRINT",FACE,{"disambiguationData":[TD([[makeQuery(id+"F0.imprint","IMPRINT",EDGE,{"derivedFrom":sQuery(id+"F0.wireOp",EDGE,"E50")}),1.0]])]});
            var Q9;
            Q9=makeQuery(id+"F0.imprint","IMPRINT",FACE,{"disambiguationData":[TD([[makeQuery(id+"F0.imprint","IMPRINT",EDGE,{"derivedFrom":sQuery(id+"F0.wireOp",EDGE,"E48")}),-1.0]])]});
            extrude(context, id + "F2", {"entities" : qUnion([Q0, Q1, Q2, Q3, Q4, Q5, Q6, Q7, Q8, Q9]), "operationType" : NewBodyOperationType.ADD, "depth" : 25 * mm});
        }
    });
